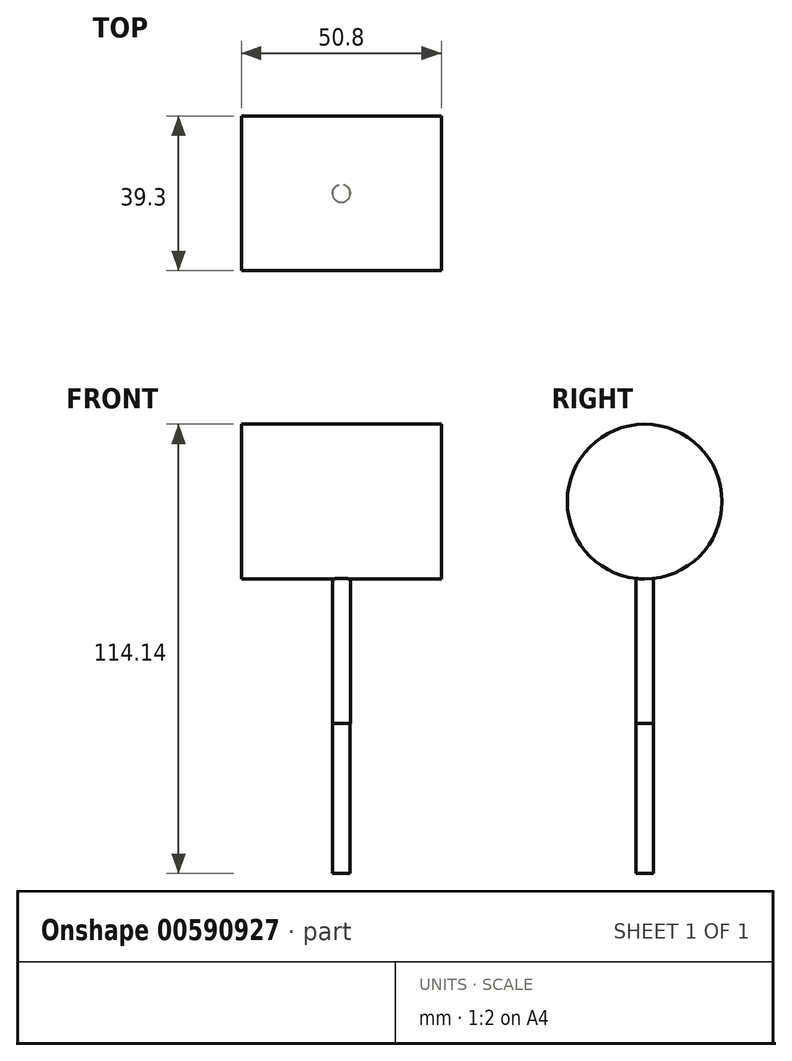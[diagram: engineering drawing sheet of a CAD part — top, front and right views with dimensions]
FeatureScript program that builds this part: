
annotation { "Feature Type Name" : "Feature", "Feature Type Description" : "" }
export const myFeature = defineFeature(function(context is Context, id is Id, definition is map)
    precondition{}
    {
        {
            var Q0;
            Q0=qCreatedBy(makeId("Right.planeOp"),FACE);
            var sketch = newSketch(context, id + "F0", { "sketchPlane" : qUnion([Q0])});
            skCircle(sketch, "E0", {"center": v(0, 56.39) * mm, "radius": 19.65 * mm});
            skSolve(sketch);
        }
        {
            var Q0;
            Q0=makeQuery(id+"F0.imprint","IMPRINT",FACE,{"disambiguationData":[TD([[makeQuery(id+"F0.imprint","IMPRINT",EDGE,{"derivedFrom":sQuery(id+"F0.wireOp",EDGE,"E0")}),1.0]])]});
            extrude(context, id + "F1", {"entities" : qUnion([Q0]), "depth" : 25.4 * mm, "offsetDistance" : 25.4 * mm});
        }
        {
            var Q0;
            Q0=makeQuery(id+"F1.opExtrude","CAP_FACE",FACE,{"disambiguationData":[OSD([sQuery(id+"F0.wireOp",EDGE,"E0")])],"isStart":true});
            extrude(context, id + "F2", {"entities" : qUnion([Q0]), "operationType" : NewBodyOperationType.ADD, "depth" : 25.4 * mm, "offsetDistance" : 25.4 * mm});
        }
        {
            var Q0;
            Q0=qCreatedBy(makeId("Top.planeOp"),FACE);
            var sketch = newSketch(context, id + "F3", { "sketchPlane" : qUnion([Q0])});
            skCircle(sketch, "E1", {"center": v(0, 0) * mm, "radius": 2.27 * mm});
            skSolve(sketch);
        }
        {
            var Q0;
            Q0=makeQuery(id+"F3.imprint","IMPRINT",FACE,{"disambiguationData":[TD([[makeQuery(id+"F3.imprint","IMPRINT",EDGE,{"derivedFrom":sQuery(id+"F3.wireOp",EDGE,"E1")}),1.0]])]});
            extrude(context, id + "F4", {"entities" : qUnion([Q0]), "operationType" : NewBodyOperationType.ADD, "depth" : 50.8 * mm, "offsetDistance" : 25.4 * mm});
        }
        {
            var Q0;
            Q0=qCreatedBy(makeId("Top.planeOp"),FACE);
            var sketch = newSketch(context, id + "F5", { "sketchPlane" : qUnion([Q0])});
            skCircle(sketch, "E2", {"center": v(0, 0) * mm, "radius": 2.25 * mm});
            skSolve(sketch);
        }
        {
            var Q0;
            Q0=makeQuery(id+"F5.imprint","IMPRINT",FACE,{"disambiguationData":[TD([[makeQuery(id+"F5.imprint","IMPRINT",EDGE,{"derivedFrom":sQuery(id+"F5.wireOp",EDGE,"E2")}),1.0]])]});
            extrude(context, id + "F6", {"entities" : qUnion([Q0]), "operationType" : NewBodyOperationType.ADD, "oppositeDirection" : true, "depth" : 38.1 * mm, "offsetDistance" : 25.4 * mm});
        }
    });
